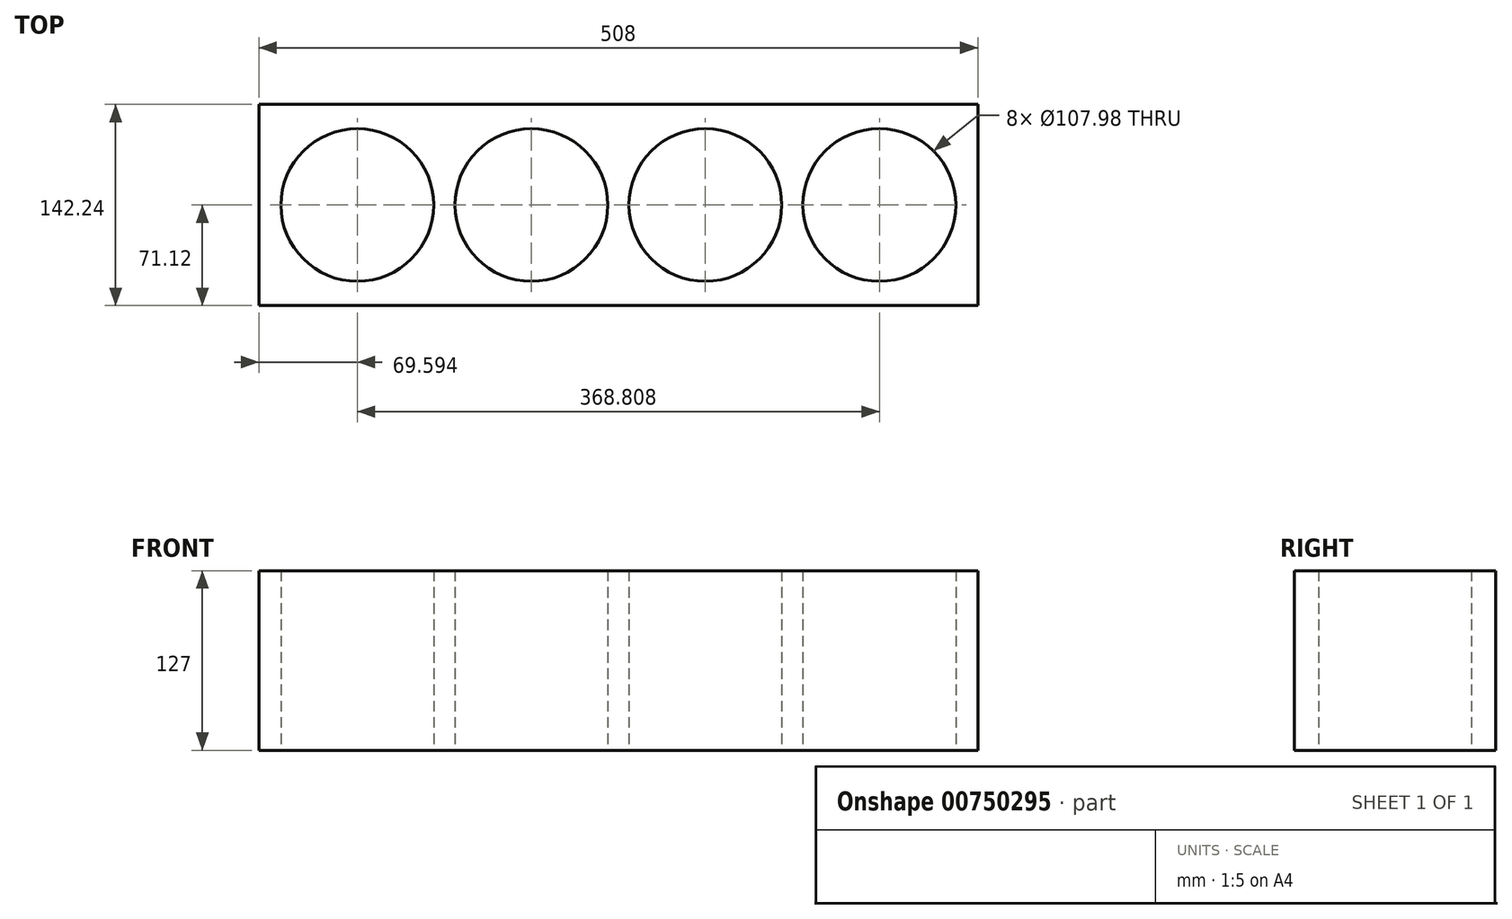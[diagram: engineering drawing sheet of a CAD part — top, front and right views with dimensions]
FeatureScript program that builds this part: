
annotation { "Feature Type Name" : "Feature", "Feature Type Description" : "" }
export const myFeature = defineFeature(function(context is Context, id is Id, definition is map)
    precondition{}
    {
        {
            var Q0;
            Q0=qCreatedBy(makeId("Top.planeOp"),FACE);
            var sketch = newSketch(context, id + "F0", { "sketchPlane" : qUnion([Q0])});
            skCircle(sketch, "E0", {"center": v(-334.73, 0) * mm, "radius": 53.99 * mm});
            skCircle(sketch, "E1.1.0.0", {"center": v(-211.79, 0) * mm, "radius": 53.99 * mm});
            skCircle(sketch, "E1.2.0.0", {"center": v(-88.85, 0) * mm, "radius": 53.99 * mm});
            skCircle(sketch, "E1.3.0.0", {"center": v(34.08, 0) * mm, "radius": 53.99 * mm});
            skLineSegment(sketch, "E1.direction1", {"start": v(-334.73, 0) * mm, "end": v(-211.79, 0) * mm, "construction": true});
            skLineSegment(sketch, "E2", {"start": v(-334.73, 0) * mm, "end": v(34.08, 0) * mm, "construction": true});
            skLineSegment(sketch, "E3.bottom", {"start": v(103.68, -71.12) * mm, "end": v(-404.32, -71.12) * mm});
            skLineSegment(sketch, "E3.top", {"start": v(103.68, 71.12) * mm, "end": v(-404.32, 71.12) * mm});
            skLineSegment(sketch, "E3.left", {"start": v(103.68, -71.12) * mm, "end": v(103.68, 71.12) * mm});
            skLineSegment(sketch, "E3.right", {"start": v(-404.32, -71.12) * mm, "end": v(-404.32, 71.12) * mm});
            skPoint(sketch, "E3.middle", {"position": v(-150.32, 0) * mm});
            skSolve(sketch);
        }
        {
            var Q0;
            Q0=makeQuery(id+"F0.imprint","IMPRINT",FACE,{"disambiguationData":[TD([[makeQuery(id+"F0.imprint","IMPRINT",EDGE,{"derivedFrom":sQuery(id+"F0.wireOp",EDGE,"E0")}),-1.0]])]});
            extrude(context, id + "F1", {"entities" : qUnion([Q0]), "depth" : 127 * mm, "offsetDistance" : 25.4 * mm});
        }
    });
